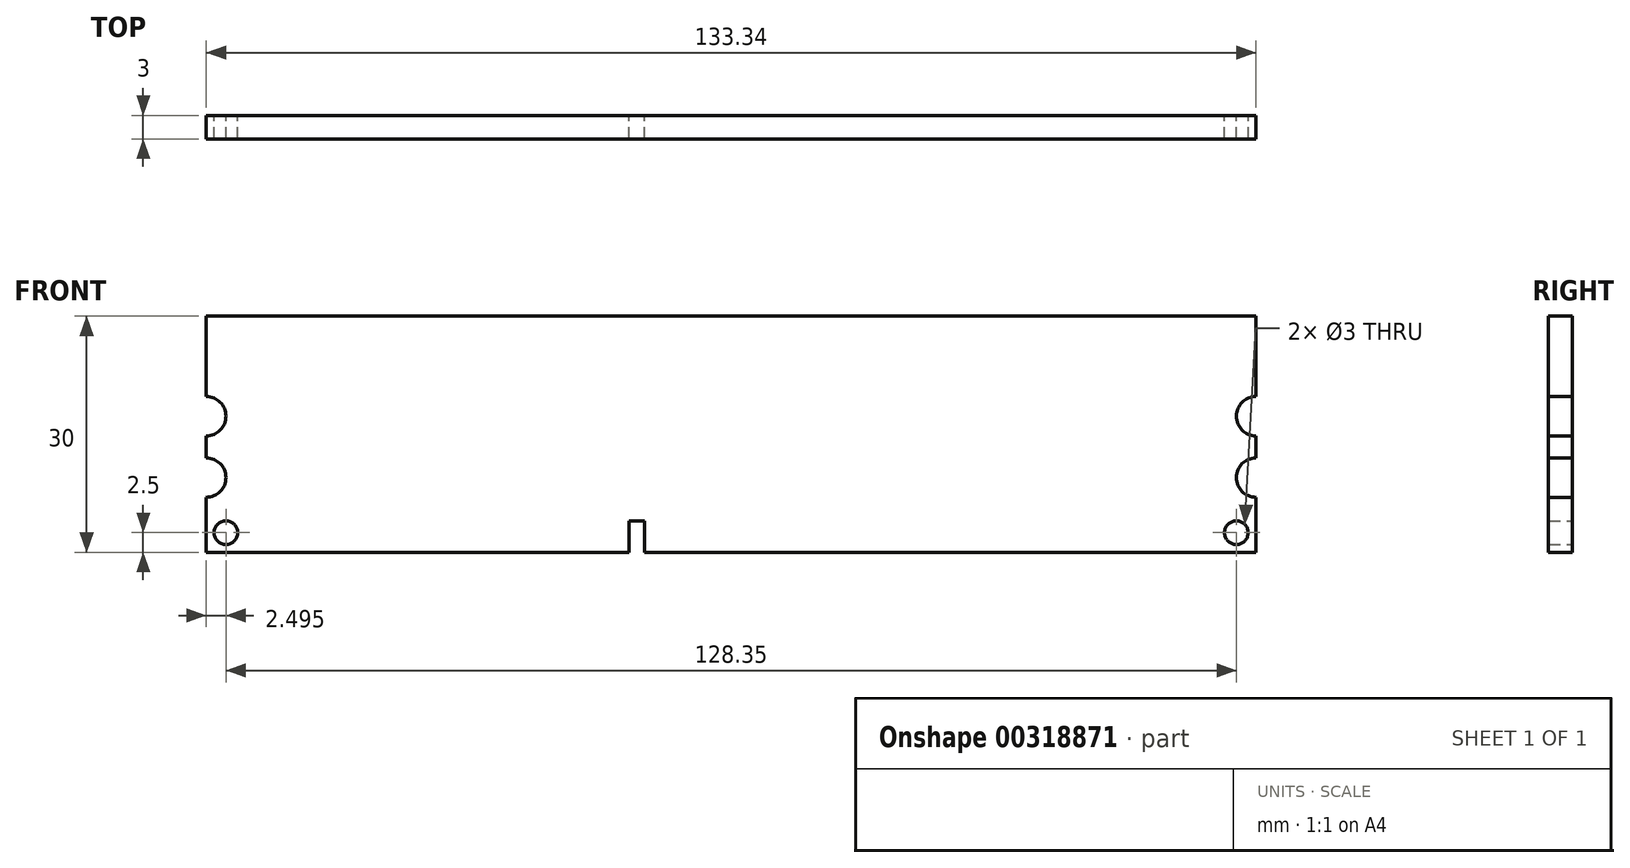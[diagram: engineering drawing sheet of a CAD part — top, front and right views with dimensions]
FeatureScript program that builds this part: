
annotation { "Feature Type Name" : "Feature", "Feature Type Description" : "" }
export const myFeature = defineFeature(function(context is Context, id is Id, definition is map)
    precondition{}
    {
        {
            var Q0;
            Q0=qCreatedBy(makeId("Front.planeOp"),FACE);
            var sketch = newSketch(context, id + "F0", { "sketchPlane" : qUnion([Q0])});
            skLineSegment(sketch, "E0.bottom", {"start": v(66.67, -15) * mm, "end": v(-66.67, -15) * mm});
            skLineSegment(sketch, "E0.top", {"start": v(66.67, 15) * mm, "end": v(-66.67, 15) * mm});
            skLineSegment(sketch, "E0.left", {"start": v(66.67, -15) * mm, "end": v(66.67, 15) * mm});
            skLineSegment(sketch, "E0.right", {"start": v(-66.67, -15) * mm, "end": v(-66.67, 15) * mm});
            skPoint(sketch, "E0.middle", {"position": v(0, 0) * mm});
            skLineSegment(sketch, "E1", {"start": v(-66.67, -15) * mm, "end": v(-66.67, -5.5) * mm});
            skLineSegment(sketch, "E2", {"start": v(-66.67, -15) * mm, "end": v(-66.67, 2.3) * mm});
            skArc(sketch, "E3", {"start": v(-66.67, 4.8) * mm, "mid": v(-64.17, 2.3) * mm, "end": v(-66.67, -0.2) * mm});
            skArc(sketch, "E4", {"start": v(-66.67, -3) * mm, "mid": v(-64.17, -5.5) * mm, "end": v(-66.67, -8) * mm});
            skArc(sketch, "E5.MirrorCS", {"start": v(66.67, 4.8) * mm, "mid": v(64.17, 2.3) * mm, "end": v(66.67, -0.2) * mm});
            skArc(sketch, "E6.MirrorCS", {"start": v(66.67, -3) * mm, "mid": v(64.17, -5.5) * mm, "end": v(66.67, -8) * mm});
            skLineSegment(sketch, "E7", {"start": v(-66.67, -15) * mm, "end": v(-12, -15) * mm});
            skLineSegment(sketch, "E8.bottom", {"start": v(-13, -11) * mm, "end": v(-11, -11) * mm});
            skLineSegment(sketch, "E8.top", {"start": v(-13, -19) * mm, "end": v(-11, -19) * mm});
            skLineSegment(sketch, "E8.left", {"start": v(-13, -11) * mm, "end": v(-13, -19) * mm});
            skLineSegment(sketch, "E8.right", {"start": v(-11, -11) * mm, "end": v(-11, -19) * mm});
            skPoint(sketch, "E8.middle", {"position": v(-12, -15) * mm});
            skCircle(sketch, "E9", {"center": v(-64.17, -12.5) * mm, "radius": 1.5 * mm});
            skCircle(sketch, "E10.MirrorC", {"center": v(64.17, -12.5) * mm, "radius": 1.5 * mm});
            skSolve(sketch);
        }
        {
            var Q0;
            {var subQ6=sQuery(id+"F0.wireOp",EDGE,"E0.top");Q0=makeQuery(id+"F0.imprint","IMPRINT",FACE,{"disambiguationData":[TD([[makeQuery(id+"F0.imprint","IMPRINT",EDGE,{"derivedFrom":subQ6}),1.0]])]});}
            extrude(context, id + "F1", {"entities" : qUnion([Q0]), "depth" : 3 * mm});
        }
    });
